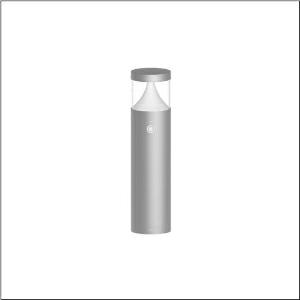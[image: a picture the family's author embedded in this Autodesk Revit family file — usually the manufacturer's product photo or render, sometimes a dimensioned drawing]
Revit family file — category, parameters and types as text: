
# Revit family: cl_31_poller_60_sensor_5cl434803
name_source: partatom
category: Lighting Fixtures
units: mm (PartAtom-declared; Revit-internal decimal feet)

## family parameters
Cut with Voids When Loaded = No
Host = Face
Light Source = No
Part Type = Normal
Room Calculation Point = No
Round Connector Dimension = Use Diameter
Shared = No

## types (1)
- --- (1 x LED, 1500 lm, 14 W, 3000K)
    Apparent Load = 14 VA
    CIE Flux Codes = 19 66 88 92 100
    Color Rendering = 80
    Color Temperature = 3000K
    Default Elevation = 1800 mm
    Description = CL 31 Bollard 60 Sensor, bollard luminaire, primary light control with lens, of PC, primary optical cover: cover panel, of PC, transparent, secondary light control with reflector, of PC, primary light characteristic: asymmetric, LED, rated luminous flux: 1.500lm, luminous efficacy: 107lm/W, light colour: 830, colour temperature: 3000K, control gear: ECG DALI, with terminal, 5-pole, max. 2.5mm², mains connection: 220..240V, AC, 50/60Hz, rated input power: 14W, luminaire housing, of aluminium, powder-coated, Siteco® metallic grey, diameter: 170mm, height: 600mm, PIR sensor, protection rating (complete): IP65, insulation class (complete): insulation class I (protective earthing), certification: CE, ENEC, impact resistance: IK08, permissible operating ambient temperature for outdoor applications: -20..+50°C, packaging unit: 1 piece
    Height = 200 mm  [stored 0.656168 ft]
    Lamp = 1 x LED
    Lamp Light Flux = 1500 lm
    Lamp Power = 14 W
    Lamp count = 1
    Length = 170 mm  [stored 0.557743 ft]
    Luminous efficacy = 107 lm/W
    Manufacturer = Siteco
    ModVariant = No
    Model = 5CL434803
    Mounting Place = Floor
    Mounting Type = Freestanding
    Number of Poles = 1
    OnlyDefault = Yes
    Power Factor = 1
    Product Name = CL 31 Poller 60 Sensor
    Product group = bollard luminaire
    ProductGroupID = 1304
    Protection Class = Protection class I
    Protection Degree = IP 65
    RLX_Detail_Level = 1
    RLX_Emergency_Light_Flux = 0 lm
    RLX_Emergency_Type = 0
    RLX_Emergency_Type_DB = No
    RlxData = <blob elided: 64221 chars, md5=48fbf3ca>
    Socket = socket
    Standby Power = 0 W
    System Light Flux = 1500 lm
    System Power = 14 W
    Type Comments = factory setting: luminous flux: 100 % | dim-lin: 254 | 350 mA
    Type Image = l_1006901.jpg
    URL = http://relux.com
    VarID = @adj_148263
    Voltage = 0 V
    Weight = 0.00 kg
    Width = 0 mm  [stored 0 ft]

note: [stored X ft] marks values corroborated as IEEE doubles in the binary element streams (Revit-internal decimal feet)

## geometry (parser evidence)
native form markers: Blend x4, Sweep x12
no freeform markers — native parametric forms only
